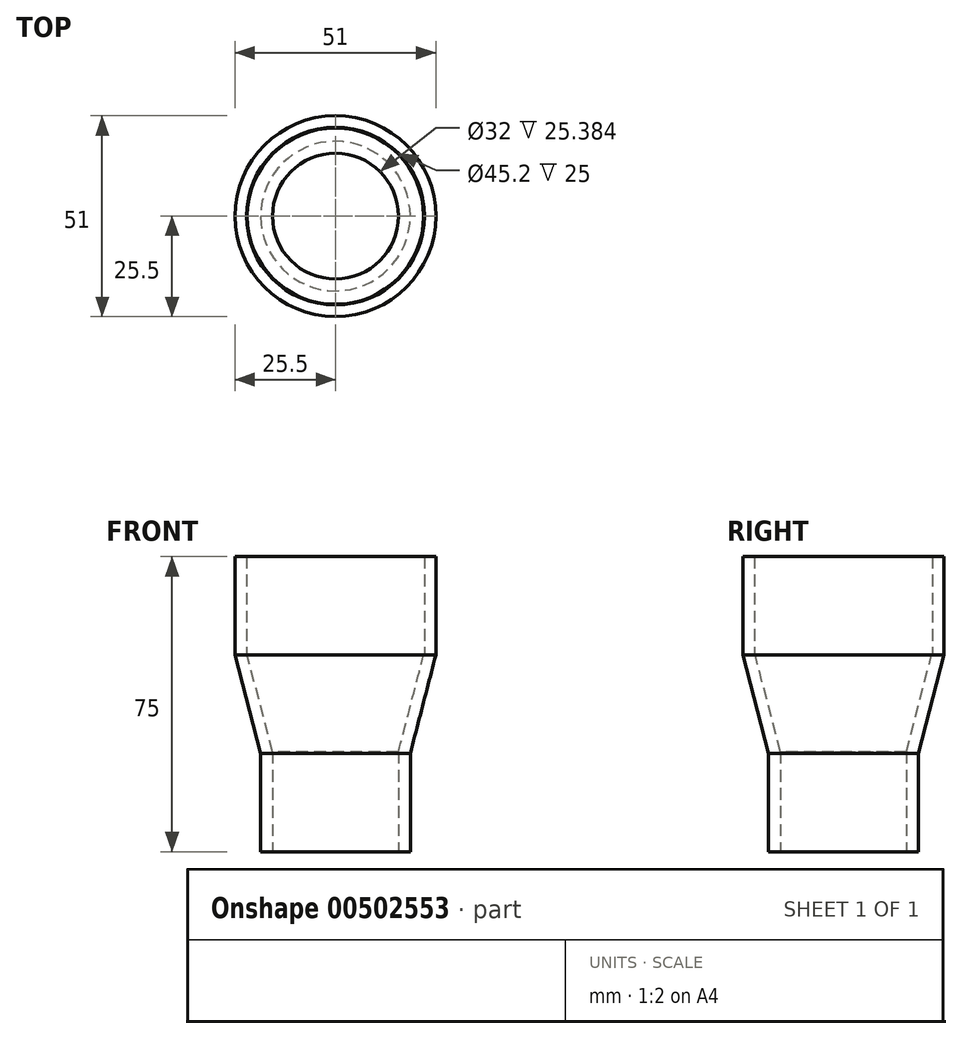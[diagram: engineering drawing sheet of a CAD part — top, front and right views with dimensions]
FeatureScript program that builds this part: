
annotation { "Feature Type Name" : "Feature", "Feature Type Description" : "" }
export const myFeature = defineFeature(function(context is Context, id is Id, definition is map)
    precondition{}
    {
        {
            var Q0;
            Q0=qCreatedBy(makeId("Top.planeOp"),FACE);
            var sketch = newSketch(context, id + "F0", { "sketchPlane" : qUnion([Q0])});
            skCircle(sketch, "E0", {"center": v(0, 0) * mm, "radius": 16 * mm});
            skCircle(sketch, "E1", {"center": v(0, 0) * mm, "radius": 19 * mm});
            skSolve(sketch);
        }
        {
            var Q0;
            Q0 = qSketchRegion(id + "F0", true);
            extrude(context, id + "F1", {"entities" : qUnion([Q0]), "depth" : 25 * mm});
        }
        {
            var Q0;
            Q0=makeQuery(id+"F1.opExtrude","CAP_FACE",FACE,{"disambiguationData":[OSD([sQuery(id+"F0.wireOp",EDGE,"E0"),sQuery(id+"F0.wireOp",EDGE,"E1")])],"isStart":false});
            var sketch = newSketch(context, id + "F2", { "sketchPlane" : qUnion([Q0])});
            skCircle(sketch, "E2", {"center": v(0, 0) * mm, "radius": 19 * mm});
            skSolve(sketch);
        }
        {
            var Q0;
            Q0=qCreatedBy(makeId("Top.planeOp"),FACE);
            cPlane(context, id + "F3", {"entities" : qUnion([Q0]), "cplaneType" : CPlaneType.OFFSET, "offset" : 50 * mm, "width" : 150 * mm, "height" : 150 * mm});
        }
        {
            var Q0;
            Q0=qCreatedBy(id+"F3.planeOp",FACE);
            var sketch = newSketch(context, id + "F4", { "sketchPlane" : qUnion([Q0])});
            skCircle(sketch, "E3", {"center": v(0, 0) * mm, "radius": 25.5 * mm});
            skSolve(sketch);
        }
        {
            var Q0;
            Q0=makeQuery(id+"F2.imprint","IMPRINT",FACE,{"disambiguationData":[TD([[makeQuery(id+"F2.imprint","IMPRINT",EDGE,{"derivedFrom":sQuery(id+"F2.wireOp",EDGE,"E2")}),1.0]])]});
            var sketch = newSketch(context, id + "F5", { "sketchPlane" : qUnion([Q0])});
            skCircle(sketch, "E4", {"center": v(0, 0) * mm, "radius": 19 * mm});
            skSolve(sketch);
        }
        {
            var Q1;
            Q1 = qSketchRegion(id + "F5", true);
            var Q2;
            Q2 = qSketchRegion(id + "F4", true);
            loft(context, id + "F6", {"operationType" : NewBodyOperationType.ADD, "sheetProfilesArray" : [{ "sheetProfileEntities" : qUnion([Q1]) }, { "sheetProfileEntities" : qUnion([Q2]) }]});
        }
        {
            var Q0;
            Q0=makeQuery(id+"F6.opLoft","CAP_FACE",FACE,{"disambiguationData":[OSD([makeQuery(id+"F4.imprint","IMPRINT",FACE,{"disambiguationData":[TD([[makeQuery(id+"F4.imprint","IMPRINT",EDGE,{"derivedFrom":sQuery(id+"F4.wireOp",EDGE,"E3")}),1.0]])]})])],"isStart":true});
            var Q1;
            Q1=makeQuery(id+"F6.opLoft","CAP_FACE",FACE,{"disambiguationData":[OSD([makeQuery(id+"F5.imprint","IMPRINT",FACE,{"disambiguationData":[TD([[makeQuery(id+"F5.imprint","IMPRINT",EDGE,{"derivedFrom":makeQuery(id+"F2.imprint","IMPRINT",EDGE,{"derivedFrom":makeQuery(id+"F1.opExtrude","CAP_EDGE",EDGE,{"disambiguationData":[OSD([sQuery(id+"F0.wireOp",EDGE,"E0")])],"isStart":false})})}),1.0]])]})])],"isStart":true});
            shell(context, id + "F7", {"entities" : qUnion([Q0, Q1]), "thickness" : 3 * mm});
        }
        {
            var Q0;
            Q0=makeQuery(id+"F6.opLoft","CAP_FACE",FACE,{"disambiguationData":[OSD([makeQuery(id+"F4.imprint","IMPRINT",FACE,{"disambiguationData":[TD([[makeQuery(id+"F4.imprint","IMPRINT",EDGE,{"derivedFrom":sQuery(id+"F4.wireOp",EDGE,"E3")}),1.0]])]})])],"isStart":true});
            var sketch = newSketch(context, id + "F8", { "sketchPlane" : qUnion([Q0])});
            skCircle(sketch, "E5", {"center": v(0, 0) * mm, "radius": 25.6 * mm});
            skCircle(sketch, "E6", {"center": v(0, 0) * mm, "radius": 22.6 * mm});
            skSolve(sketch);
        }
        {
            var Q0;
            Q0=makeQuery(id+"F8.imprint","IMPRINT",FACE,{"disambiguationData":[TD([[makeQuery(id+"F8.imprint","IMPRINT",EDGE,{"derivedFrom":sQuery(id+"F8.wireOp",EDGE,"E6")}),-1.0]])]});
            extrude(context, id + "F9", {"entities" : qUnion([Q0]), "operationType" : NewBodyOperationType.ADD, "depth" : 25 * mm, "offsetDistance" : 25 * mm});
        }
    });
